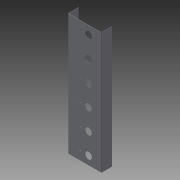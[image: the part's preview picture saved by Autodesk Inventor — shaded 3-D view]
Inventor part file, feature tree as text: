
AUTODESK INVENTOR PART (.ipt)
format: ipt  version: 2015 (Build 190159000, 159)  size: 252,928 bytes
history: native  units: mm
features: hole x21, sheet_metal_op x7, other x7, sketch x5
ambient origin geometry x8: Origin, YZ Plane, XZ Plane, XY Plane, X Axis, Y Axis, Z Axis, Center Point
bodies: Solid1 (feature_tree)
feature tree (40):
  sheet_metal_op  "Face1"
  sheet_metal_op  "Flange1"
  sheet_metal_op  "Flange2"
  hole  "Hole1"  [1 undecoded]
  hole  "Hole2"  [1 undecoded]
  hole  "Hole3"  [1 undecoded]
  hole  "Hole4"  [1 undecoded]
  hole  "Hole5"  [1 undecoded]
  hole  "Hole6"  [1 undecoded]
  hole  "Hole7"  [1 undecoded]
  hole  "Hole8"  [1 undecoded]
  hole  "Hole9"  [1 undecoded]
  hole  "Hole10"  [1 undecoded]
  hole  "Hole11"  [1 undecoded]
  hole  "Hole12"  [1 undecoded]
  hole  "Hole13"  [1 undecoded]
  hole  "Hole14"  [1 undecoded]
  hole  "Hole15"  [1 undecoded]
  hole  "Hole16"  [1 undecoded]
  hole  "Hole17"  [1 undecoded]
  hole  "Hole18"  [1 undecoded]
  hole  "Hole19"  [1 undecoded]
  other  "A-Side Definition"
  hole  "Hole20"  [1 undecoded]
  hole  "Hole21"  [1 undecoded]
  sketch  "Sketch1"  dims[d0=80.0mm d1=290.0mm]
  other  "Plate1"
  sketch  "Sketch2"  dims[d2=0.5mm d3=0.5mm]
  other  "Plate2"
  sheet_metal_op  "Bend1"
  sheet_metal_op  "Corner1"
  sketch  "Sketch3"  dims[d4=0.25mm d5=1.0mm]
  other  "Plate3"
  sheet_metal_op  "Bend2"
  sheet_metal_op  "Corner2"
  sketch  "Sketch4"  dims[d6=0.5mm d7=25.0mm d8=90.0deg d9=0.5mm]
  sketch  "Sketch5"  dims[d10=2.0mm d11=0.5mm d12=0.5mm d13=0.5mm d14=0.25mm d15=1.0mm d16=0.5mm d17=25.0mm d18=90.0deg d19=0.5mm d20=2.0mm d21=0.5mm d22=0.5mm d23=20.0mm d24=30.0mm d25=16.0mm d26=6.0mm d27=4.0mm d28=2.0mm d29=90.0deg d30=0.5mm d31=20.594885mm d32=70.0mm d33=30.0mm d34=16.0mm d35=6.0mm d36=4.0mm d37=2.0mm d38=90.0deg d39=0.5mm d40=20.594885mm d41=120.0mm d42=30.0mm d43=16.0mm d44=6.0mm d45=4.0mm d46=2.0mm d47=90.0deg d48=0.5mm d49=20.594885mm d50=170.0mm d51=30.0mm d52=16.0mm d53=6.0mm d54=4.0mm d55=2.0mm d56=90.0deg d57=0.5mm d58=20.594885mm d59=220.0mm d60=30.0mm d61=16.0mm d62=6.0mm d63=4.0mm d64=2.0mm d65=90.0deg d66=0.5mm d67=20.594885mm d68=270.0mm d69=30.0mm d70=16.0mm d71=6.0mm d72=4.0mm d73=2.0mm d74=90.0deg d75=0.5mm d76=20.594885mm d77=20.0mm d78=50.0mm d79=3.0mm d80=6.0mm d81=4.0mm d82=2.0mm d83=90.0deg d84=0.5mm d85=20.594885mm d86=70.0mm d87=50.0mm d88=3.0mm d89=6.0mm d90=4.0mm d91=2.0mm d92=90.0deg d93=0.5mm d94=20.594885mm d95=120.0mm d96=50.0mm d97=3.0mm d98=6.0mm d99=4.0mm d100=2.0mm d101=90.0deg d102=0.5mm d103=20.594885mm d104=170.0mm d105=50.0mm d106=3.0mm d107=6.0mm d108=4.0mm d109=2.0mm d110=90.0deg d111=0.5mm d112=20.594885mm d113=220.0mm d114=50.0mm d115=3.0mm d116=6.0mm d117=4.0mm d118=2.0mm d119=90.0deg d120=0.5mm d121=20.594885mm d122=270.0mm d123=50.0mm d124=3.0mm d125=6.0mm d126=4.0mm d127=2.0mm d128=90.0deg d129=0.5mm d130=20.594885mm d131=145.0mm d132=10.0mm d133=3.0mm d134=6.0mm d135=4.0mm d136=2.0mm d137=90.0deg d138=0.5mm d139=20.594885mm d140=135.0mm d141=10.0mm d142=3.0mm d143=6.0mm d144=4.0mm d145=2.0mm d146=90.0deg d147=0.5mm d148=20.594885mm d149=155.0mm d150=10.0mm d151=3.0mm d152=6.0mm d153=4.0mm d154=2.0mm d155=90.0deg d156=0.5mm d157=20.594885mm d158=40.0mm d159=12.0mm d160=10.0mm d161=6.0mm d162=4.0mm d163=2.0mm d164=90.0deg d165=0.5mm d166=20.594885mm d167=55.0mm d168=12.0mm d169=2.0mm d170=6.0mm d171=4.0mm d172=2.0mm d173=90.0deg d174=0.5mm d175=20.594885mm d176=78.0mm d177=12.0mm d178=2.0mm d179=6.0mm d180=4.0mm d181=2.0mm d182=90.0deg d183=0.5mm d184=20.594885mm d185=61.0mm d186=73.0mm d187=0.5mm d188=0.0mm d189=3.0mm d190=7.0mm d191=0.5mm d192=0.0mm d193=12.0mm d194=120.0mm d195=16.0mm d196=6.0mm d197=4.0mm d198=2.0mm d199=90.0deg d200=0.5mm d201=20.594885mm d202=12.0mm d212=108.7mm d204=3.0mm d205=6.0mm d206=4.0mm d207=2.0mm d208=90.0deg d209=0.5mm d210=20.594885mm d211=12.0mm d213=131.3mm d214=3.0mm d215=6.0mm d216=4.0mm d217=2.0mm d218=90.0deg d219=0.5mm d220=20.594885mm]
  other  "Cut1"
  other  "Cut2"
  other  "Definition1"
note: 21 required parameter values undecoded (feature->parameter linkage not recoverable at this tier; creation-order binding heuristic only, values carry confidence <= 0.55)
